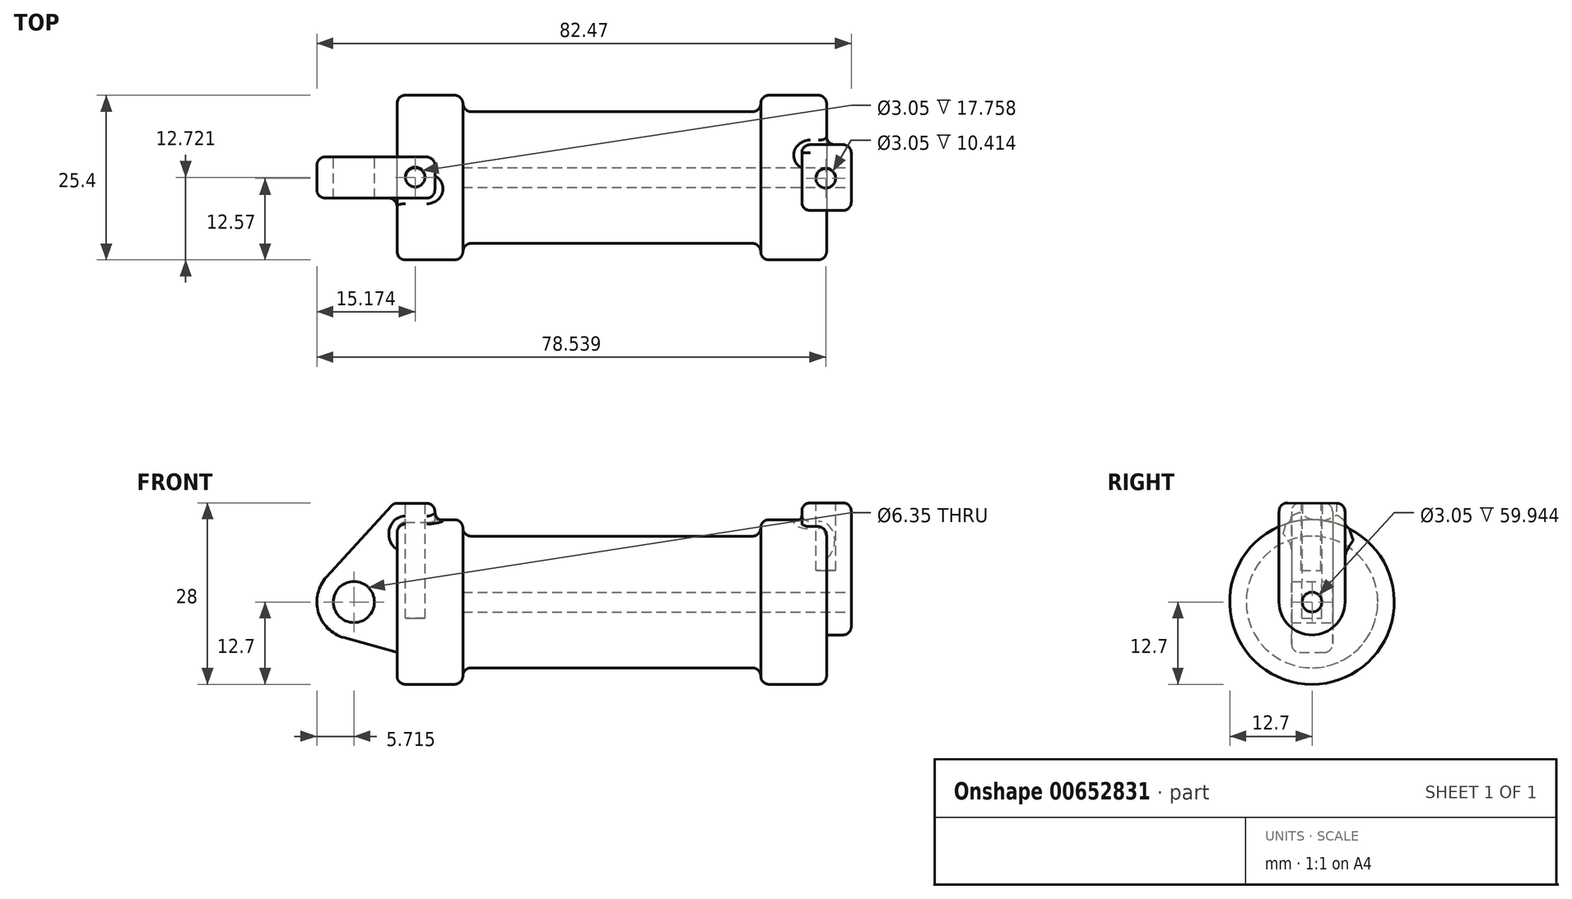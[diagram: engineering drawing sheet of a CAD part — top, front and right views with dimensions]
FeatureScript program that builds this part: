
annotation { "Feature Type Name" : "Feature", "Feature Type Description" : "" }
export const myFeature = defineFeature(function(context is Context, id is Id, definition is map)
    precondition{}
    {
        {
            var Q0;
            Q0=qCreatedBy(makeId("Front.planeOp"),FACE);
            var sketch = newSketch(context, id + "F0", { "sketchPlane" : qUnion([Q0])});
            skLineSegment(sketch, "E0", {"start": v(0, 0) * mm, "end": v(0, 12.7) * mm});
            skLineSegment(sketch, "E1", {"start": v(0, 12.7) * mm, "end": v(10.16, 12.7) * mm});
            skLineSegment(sketch, "E2", {"start": v(10.16, 12.7) * mm, "end": v(10.16, 10.16) * mm});
            skLineSegment(sketch, "E3", {"start": v(10.16, 10.16) * mm, "end": v(56.13, 10.16) * mm});
            skLineSegment(sketch, "E4", {"start": v(56.13, 10.16) * mm, "end": v(56.13, 12.7) * mm});
            skLineSegment(sketch, "E5", {"start": v(56.13, 12.7) * mm, "end": v(66.3, 12.7) * mm});
            skLineSegment(sketch, "E6", {"start": v(66.3, 12.7) * mm, "end": v(66.3, 0) * mm});
            skLineSegment(sketch, "E7", {"start": v(66.3, 0) * mm, "end": v(0, 0) * mm});
            skLineSegment(sketch, "E8", {"start": v(5.84, 15.24) * mm, "end": v(-0.5, 15.24) * mm});
            skLineSegment(sketch, "E9", {"start": v(-0.5, 15.24) * mm, "end": v(-10.88, 3.85) * mm});
            skLineSegment(sketch, "E10", {"start": v(0, 0) * mm, "end": v(-6.65, 0) * mm});
            skCircle(sketch, "E11", {"center": v(-6.65, 0) * mm, "radius": 5.72 * mm});
            skCircle(sketch, "E12", {"center": v(-6.65, 0) * mm, "radius": 3.18 * mm});
            skLineSegment(sketch, "E13", {"start": v(5.84, 15.24) * mm, "end": v(5.84, -9.4) * mm});
            skLineSegment(sketch, "E14", {"start": v(5.84, -9.4) * mm, "end": v(-8.18, -5.5) * mm});
            skSolve(sketch);
        }
        {
            var Q0;
            {var subQ0=sQuery(id+"F0.wireOp",EDGE,"E0");Q0=makeQuery(id+"F0.imprint","IMPRINT",FACE,{"disambiguationData":[TD([[makeQuery(id+"F0.imprint","IMPRINT",EDGE,{"derivedFrom":subQ0}),-1.0]])]});}
            var Q1;
            {var subQ0=sQuery(id+"F0.wireOp",EDGE,"E2");Q1=makeQuery(id+"F0.imprint","IMPRINT",FACE,{"disambiguationData":[TD([[makeQuery(id+"F0.imprint","IMPRINT",EDGE,{"derivedFrom":subQ0}),-1.0]])]});}
            var Q2;
            Q2=sQuery(id+"F0.wireOp",EDGE,"E7");
            revolve(context, id + "F1", {"entities" : qUnion([Q0, Q1]), "axis" : qUnion([Q2]), "revolveType" : RevolveType.FULL});
        }
        {
            var Q0;
            {var subQ0=sQuery(id+"F0.wireOp",EDGE,"E0");Q0=makeQuery(id+"F0.imprint","IMPRINT",FACE,{"disambiguationData":[TD([[makeQuery(id+"F0.imprint","IMPRINT",EDGE,{"derivedFrom":subQ0}),-1.0]])]});}
            var Q1;
            {var subQ1=sQuery(id+"F0.wireOp",EDGE,"E0");Q1=makeQuery(id+"F0.imprint","IMPRINT",FACE,{"disambiguationData":[TD([[makeQuery(id+"F0.imprint","IMPRINT",EDGE,{"derivedFrom":subQ1}),1.0]])]});}
            var Q2;
            {var subQ0=sQuery(id+"F0.wireOp",EDGE,"E14");Q2=makeQuery(id+"F0.imprint","IMPRINT",FACE,{"disambiguationData":[TD([[makeQuery(id+"F0.imprint","IMPRINT",EDGE,{"derivedFrom":subQ0}),-1.0]])]});}
            var Q3;
            {var subQ5=sQuery(id+"F0.wireOp",EDGE,"E12");Q3=makeQuery(id+"F0.imprint","IMPRINT",FACE,{"disambiguationData":[TD([[makeQuery(id+"F0.imprint","IMPRINT",EDGE,{"derivedFrom":subQ5}),-1.0]])]});}
            extrude(context, id + "F2", {"entities" : qUnion([Q0, Q1, Q2, Q3]), "operationType" : NewBodyOperationType.ADD, "endBound" : BoundingType.SYMMETRIC, "depth" : 6.35 * mm, "offsetDistance" : 25.4 * mm});
        }
        {
            var Q0;
            Q0=makeQuery(id+"F1.opRevolve","SWEPT_FACE",FACE,{"disambiguationData":[OSD([sQuery(id+"F0.wireOp",EDGE,"E6")])]});
            var sketch = newSketch(context, id + "F3", { "sketchPlane" : qUnion([Q0])});
            skCircle(sketch, "E15", {"center": v(0, 0) * mm, "radius": 5.08 * mm});
            skCircle(sketch, "E16", {"center": v(0, 0) * mm, "radius": 1.52 * mm});
            skLineSegment(sketch, "E17", {"start": v(-5.08, 0) * mm, "end": v(-5.08, 15.3) * mm});
            skLineSegment(sketch, "E18", {"start": v(5.08, 0) * mm, "end": v(5.08, 15.24) * mm});
            skLineSegment(sketch, "E19", {"start": v(5.08, 15.24) * mm, "end": v(-5.08, 15.3) * mm});
            skSolve(sketch);
        }
        {
            var Q0;
            Q0=makeQuery(id+"F3.imprint","IMPRINT",FACE,{"disambiguationData":[TD([[makeQuery(id+"F3.imprint","IMPRINT",EDGE,{"derivedFrom":sQuery(id+"F3.wireOp",EDGE,"E16")}),-1.0]])]});
            var Q1;
            {var subQ0=sQuery(id+"F3.wireOp",EDGE,"E19");Q1=makeQuery(id+"F3.imprint","IMPRINT",FACE,{"disambiguationData":[TD([[makeQuery(id+"F3.imprint","IMPRINT",EDGE,{"derivedFrom":subQ0}),1.0]])]});}
            var Q2;
            {var subQ0=sQuery(id+"F3.wireOp",EDGE,"E17");var subQ1=sQuery(id+"F3.wireOp",EDGE,"E15");var subQ2=makeQuery(id+"F3.imprint","INTERSECT",VERTEX,{"derivedFrom":[subQ1,subQ0]});Q2=makeQuery(id+"F3.imprint","IMPRINT",FACE,{"disambiguationData":[TD([[makeQuery(id+"F3.imprint","IMPRINT",EDGE,{"disambiguationData":[TD([[subQ2,1.0]])],"derivedFrom":subQ1}),-1.0]])]});}
            extrude(context, id + "F4", {"entities" : qUnion([Q0, Q1, Q2]), "operationType" : NewBodyOperationType.ADD, "endBound" : BoundingType.SYMMETRIC, "oppositeDirection" : true, "depth" : 7.62 * mm, "offsetDistance" : 25.4 * mm});
        }
        {
            var Q0;
            Q0=makeQuery(id+"F4.opExtrude","SWEPT_FACE",FACE,{"disambiguationData":[OSD([sQuery(id+"F3.wireOp",EDGE,"E19")])]});
            var sketch = newSketch(context, id + "F5", { "sketchPlane" : qUnion([Q0])});
            skCircle(sketch, "E20", {"center": v(66.17, -0.2) * mm, "radius": 1.52 * mm});
            skCircle(sketch, "E21", {"center": v(2.8, -0.02) * mm, "radius": 1.52 * mm});
            skSolve(sketch);
        }
        {
            var Q0;
            Q0=makeQuery(id+"F5.imprint","IMPRINT",FACE,{"disambiguationData":[TD([[makeQuery(id+"F5.imprint","IMPRINT",EDGE,{"derivedFrom":sQuery(id+"F5.wireOp",EDGE,"E21")}),1.0]])]});
            extrude(context, id + "F6", {"entities" : qUnion([Q0]), "operationType" : NewBodyOperationType.REMOVE, "oppositeDirection" : true, "depth" : 17.78 * mm, "offsetDistance" : 25.4 * mm});
        }
        {
            var Q0;
            Q0=makeQuery(id+"F5.imprint","IMPRINT",FACE,{"disambiguationData":[TD([[makeQuery(id+"F5.imprint","IMPRINT",EDGE,{"derivedFrom":sQuery(id+"F5.wireOp",EDGE,"E20")}),1.0]])]});
            extrude(context, id + "F7", {"entities" : qUnion([Q0]), "operationType" : NewBodyOperationType.REMOVE, "oppositeDirection" : true, "depth" : 10.4 * mm, "offsetDistance" : 25.4 * mm});
        }
        {
            var Q0;
            Q0=makeQuery(id+"F4.boolean.opBoolean","SPLIT",FACE,{"disambiguationData":[TD([makeQuery(id+"F4.opExtrude","SWEPT_FACE",FACE,{"disambiguationData":[OSD([sQuery(id+"F3.wireOp",EDGE,"E16")])]})])],"derivedFrom":makeQuery(id+"F1.opRevolve","SWEPT_FACE",FACE,{"disambiguationData":[OSD([sQuery(id+"F0.wireOp",EDGE,"E6")])]})});
            var Q1;
            Q1=makeQuery(id+"F1.opRevolve","SWEPT_FACE",FACE,{"disambiguationData":[OSD([sQuery(id+"F0.wireOp",EDGE,"E2")])]});
            extrude(context, id + "F8", {"entities" : qUnion([Q0]), "operationType" : NewBodyOperationType.REMOVE, "endBound" : BoundingType.UP_TO_SURFACE, "oppositeDirection" : true, "depth" : 25.4 * mm, "endBoundEntityFace" : qUnion([Q1]), "offsetDistance" : 25.4 * mm});
        }
        {
            var Q0;
            Q0=makeQuery(id+"F1.opRevolve","SWEPT_EDGE",EDGE,{"disambiguationData":[OSD([sQuery(id+"F0.wireOp",EDGE,"E1"),sQuery(id+"F0.wireOp",EDGE,"E2")])]});
            var Q1;
            Q1=makeQuery(id+"F1.opRevolve","SWEPT_EDGE",EDGE,{"disambiguationData":[OSD([sQuery(id+"F0.wireOp",EDGE,"E2"),sQuery(id+"F0.wireOp",EDGE,"E3")])]});
            var Q2;
            Q2=makeQuery(id+"F2.opExtrude","SWEPT_EDGE",EDGE,{"disambiguationData":[OSD([sQuery(id+"F0.wireOp",EDGE,"E8"),sQuery(id+"F0.wireOp",EDGE,"E13")])]});
            var Q3;
            Q3=makeQuery(id+"F2.opExtrude","CAP_EDGE",EDGE,{"disambiguationData":[OSD([sQuery(id+"F0.wireOp",EDGE,"E8")])],"isStart":false});
            var Q4;
            Q4=makeQuery(id+"F2.opExtrude","CAP_EDGE",EDGE,{"disambiguationData":[OSD([sQuery(id+"F0.wireOp",EDGE,"E13")])],"isStart":false});
            var Q5;
            Q5=makeQuery(id+"F2.boolean.opBoolean","INTERSECT",EDGE,{"derivedFrom":[makeQuery(id+"F1.opRevolve","SWEPT_FACE",FACE,{"disambiguationData":[OSD([sQuery(id+"F0.wireOp",EDGE,"E1")])]}),makeQuery(id+"F2.opExtrude","CAP_FACE",FACE,{"disambiguationData":[OSD([sQuery(id+"F0.wireOp",EDGE,"E8"),sQuery(id+"F0.wireOp",EDGE,"E9"),sQuery(id+"F0.wireOp",EDGE,"E11"),sQuery(id+"F0.wireOp",EDGE,"E12"),sQuery(id+"F0.wireOp",EDGE,"E13"),sQuery(id+"F0.wireOp",EDGE,"E14")])],"isStart":false})]});
            var Q6;
            Q6=makeQuery(id+"F2.opExtrude","CAP_EDGE",EDGE,{"disambiguationData":[OSD([sQuery(id+"F0.wireOp",EDGE,"E9")])],"isStart":false});
            var Q7;
            Q7=makeQuery(id+"F2.opExtrude","SWEPT_EDGE",EDGE,{"disambiguationData":[OSD([sQuery(id+"F0.wireOp",EDGE,"E8"),sQuery(id+"F0.wireOp",EDGE,"E9")])]});
            var Q8;
            Q8=makeQuery(id+"F1.opRevolve","SWEPT_EDGE",EDGE,{"disambiguationData":[OSD([sQuery(id+"F0.wireOp",EDGE,"E0"),sQuery(id+"F0.wireOp",EDGE,"E1")])]});
            var Q9;
            Q9=makeQuery(id+"F2.opExtrude","CAP_EDGE",EDGE,{"disambiguationData":[OSD([sQuery(id+"F0.wireOp",EDGE,"E9")])],"isStart":true});
            var Q10;
            Q10=makeQuery(id+"F1.opRevolve","SWEPT_EDGE",EDGE,{"disambiguationData":[OSD([sQuery(id+"F0.wireOp",EDGE,"E4"),sQuery(id+"F0.wireOp",EDGE,"E5")])]});
            var Q11;
            Q11=makeQuery(id+"F1.opRevolve","SWEPT_EDGE",EDGE,{"disambiguationData":[OSD([sQuery(id+"F0.wireOp",EDGE,"E3"),sQuery(id+"F0.wireOp",EDGE,"E4")])]});
            var Q12;
            Q12=makeQuery(id+"F1.opRevolve","SWEPT_EDGE",EDGE,{"disambiguationData":[OSD([sQuery(id+"F0.wireOp",EDGE,"E5"),sQuery(id+"F0.wireOp",EDGE,"E6")])]});
            var Q13;
            Q13=makeQuery(id+"F4.opExtrude","CAP_EDGE",EDGE,{"disambiguationData":[OSD([sQuery(id+"F3.wireOp",EDGE,"E17")])],"isStart":false});
            var Q14;
            Q14=makeQuery(id+"F4.opExtrude","SWEPT_EDGE",EDGE,{"disambiguationData":[OSD([sQuery(id+"F3.wireOp",EDGE,"E17"),sQuery(id+"F3.wireOp",EDGE,"E19")])]});
            var Q15;
            Q15=makeQuery(id+"F4.opExtrude","CAP_EDGE",EDGE,{"disambiguationData":[OSD([sQuery(id+"F3.wireOp",EDGE,"E19")])],"isStart":false});
            var Q16;
            Q16=makeQuery(id+"F4.opExtrude","CAP_EDGE",EDGE,{"disambiguationData":[OSD([sQuery(id+"F3.wireOp",EDGE,"E17")])],"isStart":true});
            var Q17;
            Q17=makeQuery(id+"F4.opExtrude","CAP_EDGE",EDGE,{"disambiguationData":[OSD([sQuery(id+"F3.wireOp",EDGE,"E18")])],"isStart":true});
            var Q18;
            Q18=makeQuery(id+"F2.opExtrude","CAP_EDGE",EDGE,{"disambiguationData":[OSD([sQuery(id+"F0.wireOp",EDGE,"E8")])],"isStart":true});
            var Q19;
            Q19=makeQuery(id+"F2.opExtrude","CAP_EDGE",EDGE,{"disambiguationData":[OSD([sQuery(id+"F0.wireOp",EDGE,"E13")])],"isStart":true});
            var Q20;
            Q20=makeQuery(id+"F4.opExtrude","CAP_EDGE",EDGE,{"disambiguationData":[OSD([sQuery(id+"F3.wireOp",EDGE,"E19")])],"isStart":true});
            var Q21;
            Q21=makeQuery(id+"F4.opExtrude","SWEPT_EDGE",EDGE,{"disambiguationData":[OSD([sQuery(id+"F3.wireOp",EDGE,"E18"),sQuery(id+"F3.wireOp",EDGE,"E19")])]});
            var Q22;
            Q22=makeQuery(id+"F4.opExtrude","CAP_EDGE",EDGE,{"disambiguationData":[OSD([sQuery(id+"F3.wireOp",EDGE,"E18")])],"isStart":false});
            var Q23;
            Q23=makeQuery(id+"F4.boolean.opBoolean","INTERSECT",EDGE,{"derivedFrom":[makeQuery(id+"F1.opRevolve","SWEPT_FACE",FACE,{"disambiguationData":[OSD([sQuery(id+"F0.wireOp",EDGE,"E5")])]}),makeQuery(id+"F4.opExtrude","SWEPT_FACE",FACE,{"disambiguationData":[OSD([sQuery(id+"F3.wireOp",EDGE,"E18")])]})]});
            fillet(context, id + "F9", {"entities" : qUnion([Q0, Q1, Q2, Q3, Q4, Q5, Q6, Q7, Q8, Q9, Q10, Q11, Q12, Q13, Q14, Q15, Q16, Q17, Q18, Q19, Q20, Q21, Q22, Q23]), "radius" : 1.27 * mm, "tangentPropagation" : true, "allowEdgeOverflow" : false});
        }
    });
